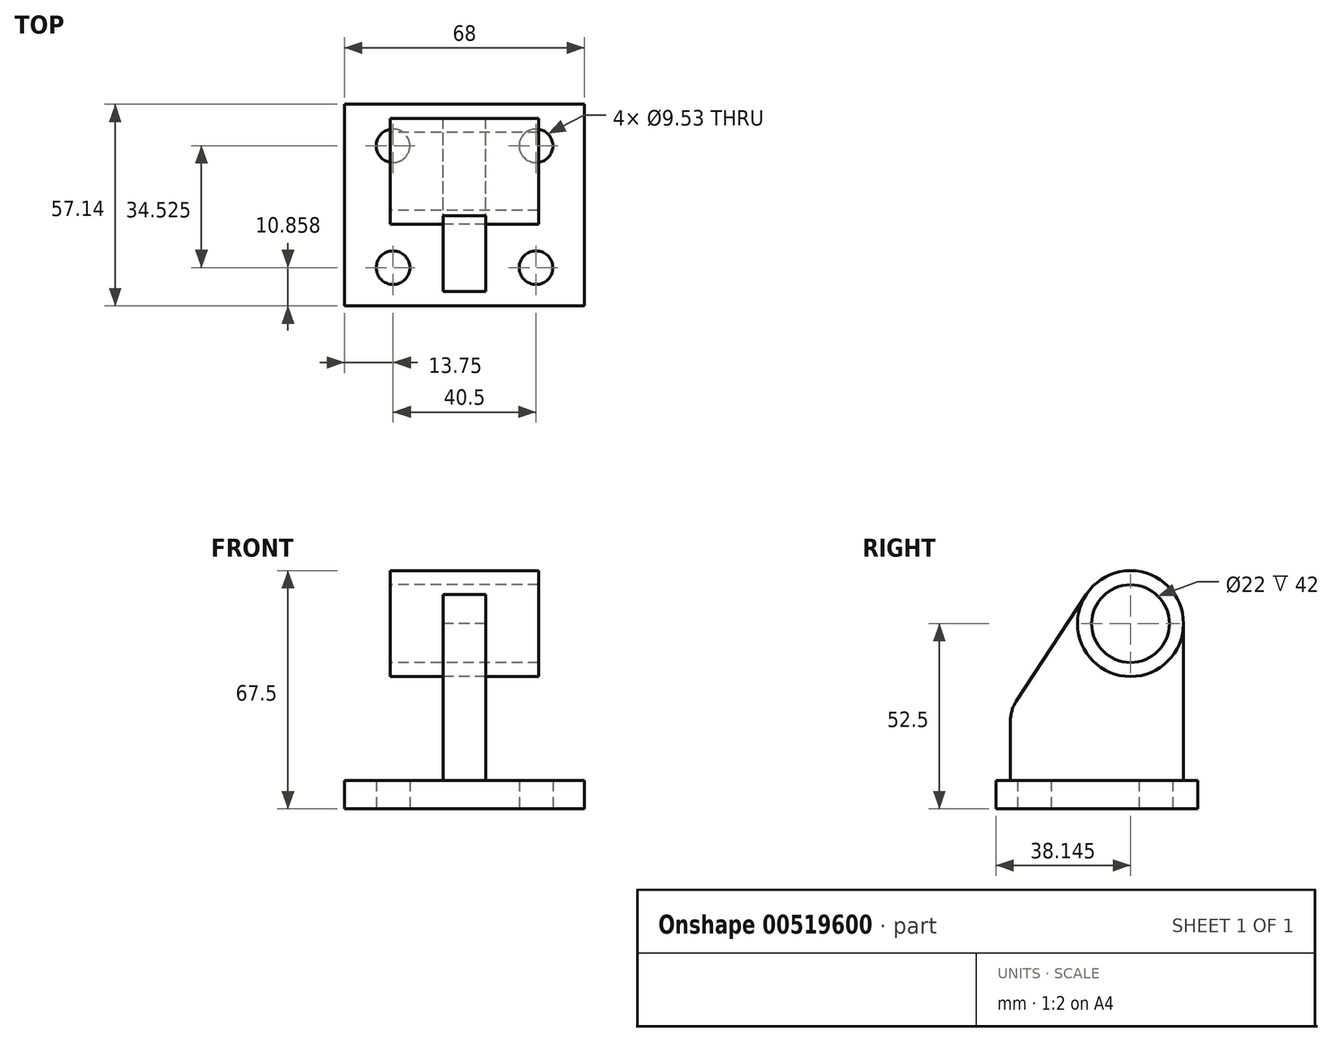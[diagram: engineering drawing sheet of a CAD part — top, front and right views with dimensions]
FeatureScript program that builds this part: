
annotation { "Feature Type Name" : "Feature", "Feature Type Description" : "" }
export const myFeature = defineFeature(function(context is Context, id is Id, definition is map)
    precondition{}
    {
        {
            var Q0;
            Q0=qCreatedBy(makeId("Top.planeOp"),FACE);
            var sketch = newSketch(context, id + "F0", { "sketchPlane" : qUnion([Q0])});
            skLineSegment(sketch, "E0.bottom", {"start": v(-34, 28.58) * mm, "end": v(34, 28.58) * mm});
            skLineSegment(sketch, "E0.top", {"start": v(-34, -28.57) * mm, "end": v(34, -28.57) * mm});
            skLineSegment(sketch, "E0.left", {"start": v(-34, 28.58) * mm, "end": v(-34, -28.57) * mm});
            skLineSegment(sketch, "E0.right", {"start": v(34, 28.58) * mm, "end": v(34, -28.57) * mm});
            skPoint(sketch, "E0.middle", {"position": v(0, 0) * mm});
            skCircle(sketch, "E1", {"center": v(-20.25, 16.81) * mm, "radius": 4.76 * mm});
            skCircle(sketch, "E2", {"center": v(20.25, 16.81) * mm, "radius": 4.76 * mm});
            skCircle(sketch, "E3", {"center": v(20.25, -17.71) * mm, "radius": 4.76 * mm});
            skCircle(sketch, "E4", {"center": v(-20.25, -17.71) * mm, "radius": 4.76 * mm});
            skPoint(sketch, "E5", {"position": v(-20.25, 21.58) * mm});
            skSolve(sketch);
        }
        {
            var Q0;
            Q0 = qSketchRegion(id + "F0", true);
            extrude(context, id + "F1", {"entities" : qUnion([Q0]), "depth" : 8 * mm, "offsetDistance" : 25 * mm});
        }
        {
            var Q0;
            Q0=qCreatedBy(makeId("Right.planeOp"),FACE);
            var sketch = newSketch(context, id + "F2", { "sketchPlane" : qUnion([Q0])});
            skCircle(sketch, "E6", {"center": v(9.58, 52.5) * mm, "radius": 15 * mm});
            skCircle(sketch, "E7", {"center": v(9.58, 52.5) * mm, "radius": 11 * mm});
            skPoint(sketch, "E8", {"position": v(9.58, 67.5) * mm});
            skSolve(sketch);
        }
        {
            var Q0;
            Q0 = qSketchRegion(id + "F2", true);
            extrude(context, id + "F3", {"entities" : qUnion([Q0]), "endBound" : BoundingType.SYMMETRIC, "depth" : 42 * mm, "offsetDistance" : 25 * mm});
        }
        {
            var Q0;
            Q0=qCreatedBy(makeId("Right.planeOp"),FACE);
            var sketch = newSketch(context, id + "F4", { "sketchPlane" : qUnion([Q0])});
            skArc(sketch, "E9", {"start": v(-2.97, 60.72) * mm, "mid": v(5.28, 38.13) * mm, "end": v(24.58, 52.5) * mm});
            skLineSegment(sketch, "E10", {"start": v(24.58, 52.5) * mm, "end": v(24.58, 8) * mm});
            skLineSegment(sketch, "E11", {"start": v(-24.42, 8) * mm, "end": v(-24.42, 25.01) * mm});
            skLineSegment(sketch, "E12", {"start": v(-22.79, 30.5) * mm, "end": v(-2.97, 60.72) * mm});
            skLineSegment(sketch, "E13", {"start": v(-24.42, 8) * mm, "end": v(24.58, 8) * mm});
            skPoint(sketch, "E14.visualSharp", {"position": v(-24.42, 28) * mm});
            skArc(sketch, "E14.filletArc", {"start": v(-22.79, 30.5) * mm, "mid": v(-24, 27.88) * mm, "end": v(-24.42, 25.01) * mm});
            skSolve(sketch);
        }
        {
            var Q0;
            Q0 = qSketchRegion(id + "F4", true);
            extrude(context, id + "F5", {"entities" : qUnion([Q0]), "endBound" : BoundingType.SYMMETRIC, "depth" : 12 * mm, "offsetDistance" : 25 * mm});
        }
    });
